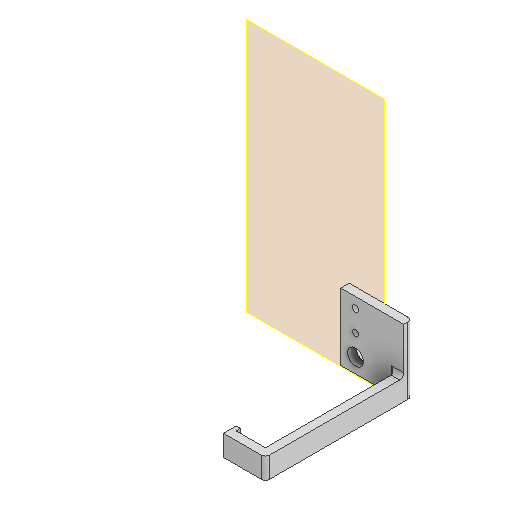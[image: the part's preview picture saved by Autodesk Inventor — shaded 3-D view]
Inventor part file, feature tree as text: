
AUTODESK INVENTOR PART (.ipt)
format: ipt  version: 2022 (Build 260153000, 153)  size: 145,920 bytes
history: native  units: in
note: dims shown in document units (in); Inventor stores cm internally (conversion verified against a paired STEP export)
features: extrude x3, sketch x3, other x2, plane x1, fillet x1, reference x1, projected_geometry x1
ambient origin geometry x8: Origin, YZ Plane, XZ Plane, XY Plane, X Axis, Y Axis, Z Axis, Center Point
bodies: Solid1 (feature_tree)
feature tree (12):
  plane  "Work Plane1"
  extrude  "Extrusion1"  Depth=1.2598in
  extrude  "Extrusion2"  Depth=0.1575in TaperAngle=0.0deg
  fillet  "Fillet1"  Radius=0.1575in
  extrude  "Extrusion3"  Depth=0.7874in
  sketch  "Sketch1"  dims[d0=1.1811in d1=1.2598in]
  reference  "Reference1"
  sketch  "Sketch2"  dims[d2=0.1969in d3=0.1575in d4=0.0in d5=0.1575in]
  projected_geometry  "Projected Loop1"
  sketch  "Sketch3"  dims[d6=2.4409in d7=0.7874in d8=0.1575in d9=0.3937in d10=0.0in d11=0.0787in d12=0.0787in d13=0.0787in d14=0.3937in d15=0.0in]
  other  "Assembly_XY_stage_with_motors_v3.iam"
  other  "30_XY_Sample_lightsheetarm_v3:1"
